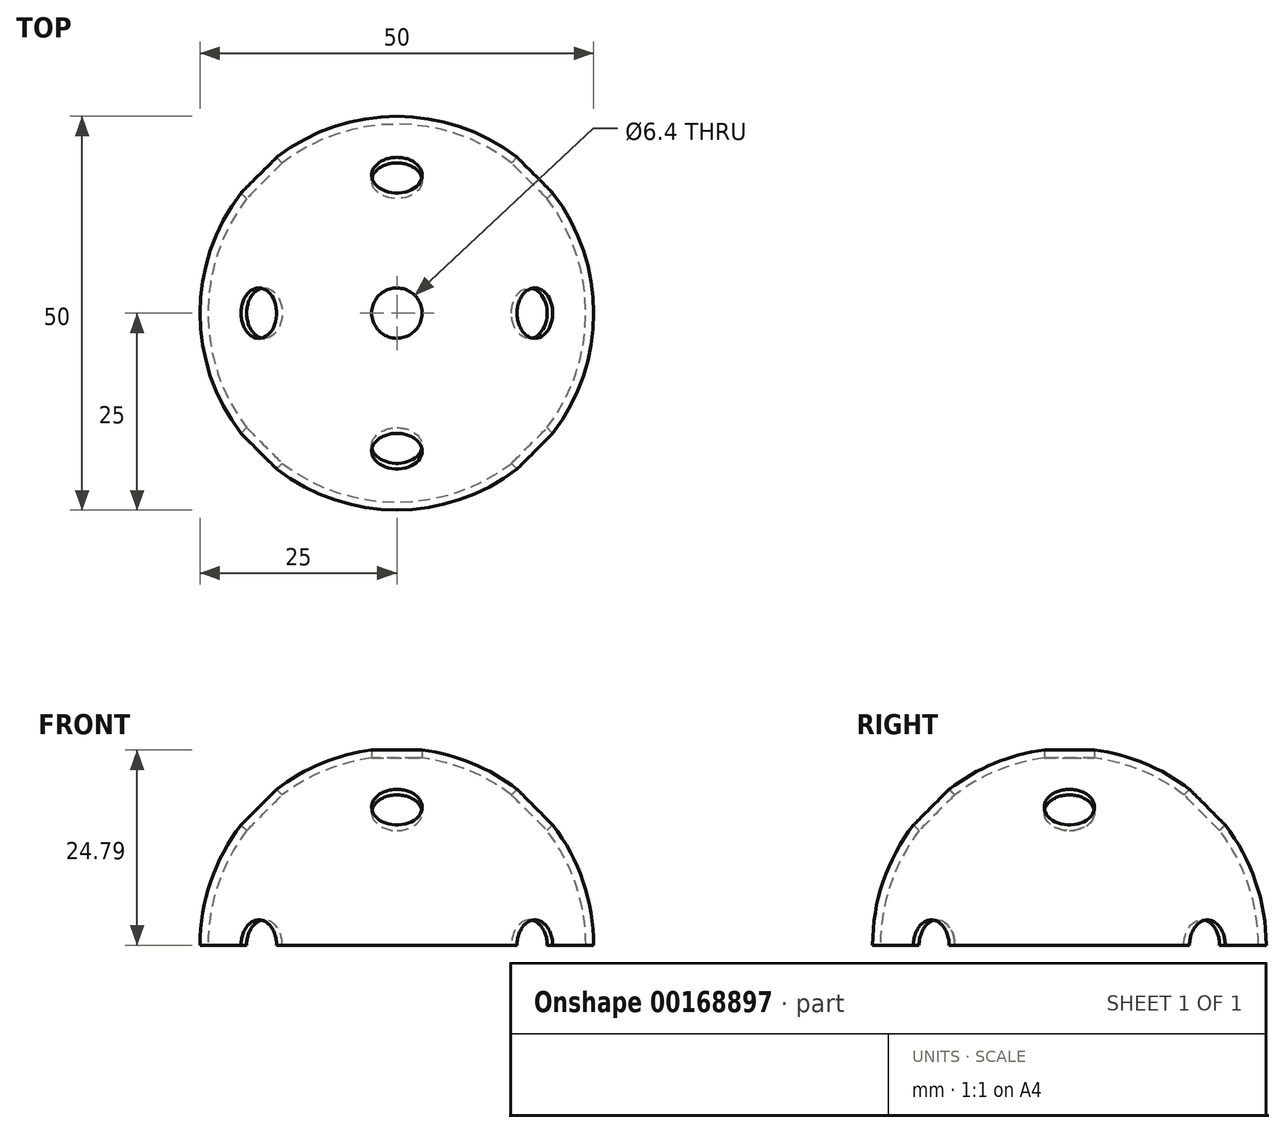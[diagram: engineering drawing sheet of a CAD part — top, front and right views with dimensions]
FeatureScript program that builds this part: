
annotation { "Feature Type Name" : "Feature", "Feature Type Description" : "" }
export const myFeature = defineFeature(function(context is Context, id is Id, definition is map)
    precondition{}
    {
        {
            var Q0;
            Q0=qCreatedBy(makeId("Front.planeOp"),FACE);
            var sketch = newSketch(context, id + "F0", { "sketchPlane" : qUnion([Q0])});
            skLineSegment(sketch, "E0", {"start": v(0, 25) * mm, "end": v(0, 0) * mm});
            skArc(sketch, "E1", {"start": v(0, 25) * mm, "mid": v(17.68, 17.68) * mm, "end": v(25, 0) * mm});
            skLineSegment(sketch, "E2", {"start": v(25, 0) * mm, "end": v(0, 0) * mm});
            skSolve(sketch);
        }
        {
            var Q0;
            Q0=makeQuery(id+"F0.imprint","IMPRINT",FACE,{"disambiguationData":[TD([[makeQuery(id+"F0.imprint","IMPRINT",EDGE,{"derivedFrom":sQuery(id+"F0.wireOp",EDGE,"E0")}),1.0]])]});
            var Q1;
            Q1=sQuery(id+"F0.wireOp",EDGE,"E0");
            revolve(context, id + "F1", {"entities" : qUnion([Q0]), "axis" : qUnion([Q1]), "revolveType" : RevolveType.FULL});
        }
        {
            var Q0;
            Q0=makeQuery(id+"F1.opRevolve","SWEPT_FACE",FACE,{"disambiguationData":[OSD([sQuery(id+"F0.wireOp",EDGE,"E2")])]});
            shell(context, id + "F2", {"entities" : qUnion([Q0]), "thickness" : 1 * mm});
        }
        {
            var Q0;
            Q0=qCreatedBy(makeId("Top.planeOp"),FACE);
            var sketch = newSketch(context, id + "F3", { "sketchPlane" : qUnion([Q0])});
            skCircle(sketch, "E3", {"center": v(0, 0) * mm, "radius": 3.2 * mm});
            skSolve(sketch);
        }
        {
            var Q0;
            Q0=makeQuery(id+"F3.imprint","IMPRINT",FACE,{"disambiguationData":[TD([[makeQuery(id+"F3.imprint","IMPRINT",EDGE,{"derivedFrom":sQuery(id+"F3.wireOp",EDGE,"E3")}),1.0]])]});
            extrude(context, id + "F4", {"entities" : qUnion([Q0]), "operationType" : NewBodyOperationType.REMOVE, "endBound" : BoundingType.THROUGH_ALL, "depth" : 25 * mm});
        }
        {
            var Q0;
            Q0=qCreatedBy(makeId("Right.planeOp"),FACE);
            var Q1;
            Q1=qCreatedBy(makeId("Top.planeOp"),FACE);
            cPlane(context, id + "F5", {"entities" : qUnion([Q0, Q1]), "cplaneType" : CPlaneType.MID_PLANE, "offset" : 25 * mm, "width" : 150 * mm, "height" : 150 * mm});
        }
        {
            var Q0;
            Q0=qCreatedBy(id+"F5.planeOp",FACE);
            var sketch = newSketch(context, id + "F6", { "sketchPlane" : qUnion([Q0])});
            skCircle(sketch, "E4", {"center": v(0, 0) * mm, "radius": 3.2 * mm});
            skSolve(sketch);
        }
        {
            var Q0;
            Q0=makeQuery(id+"F6.imprint","IMPRINT",FACE,{"disambiguationData":[TD([[makeQuery(id+"F6.imprint","IMPRINT",EDGE,{"derivedFrom":sQuery(id+"F6.wireOp",EDGE,"E4")}),1.0]])]});
            extrude(context, id + "F7", {"entities" : qUnion([Q0]), "operationType" : NewBodyOperationType.REMOVE, "endBound" : BoundingType.THROUGH_ALL, "oppositeDirection" : true, "depth" : 25 * mm});
        }
        {
            var Q0;
            Q0=qCreatedBy(makeId("Front.planeOp"),FACE);
            var Q1;
            Q1=qCreatedBy(makeId("Top.planeOp"),FACE);
            cPlane(context, id + "F8", {"entities" : qUnion([Q0, Q1]), "cplaneType" : CPlaneType.MID_PLANE, "offset" : 25 * mm, "width" : 150 * mm, "height" : 150 * mm});
        }
        {
            var Q0;
            Q0=qCreatedBy(id+"F8.planeOp",FACE);
            var sketch = newSketch(context, id + "F9", { "sketchPlane" : qUnion([Q0])});
            skCircle(sketch, "E5", {"center": v(0, 0) * mm, "radius": 3.2 * mm});
            skSolve(sketch);
        }
        {
            var Q0;
            Q0=makeQuery(id+"F9.imprint","IMPRINT",FACE,{"disambiguationData":[TD([[makeQuery(id+"F9.imprint","IMPRINT",EDGE,{"derivedFrom":sQuery(id+"F9.wireOp",EDGE,"E5")}),1.0]])]});
            extrude(context, id + "F10", {"entities" : qUnion([Q0]), "operationType" : NewBodyOperationType.REMOVE, "endBound" : BoundingType.THROUGH_ALL, "oppositeDirection" : true, "depth" : 25 * mm});
        }
        {
            var Q0;
            Q0=qCreatedBy(makeId("Top.planeOp"),FACE);
            var Q1;
            Q1=qCreatedBy(makeId("Right.planeOp"),FACE);
            cPlane(context, id + "F11", {"entities" : qUnion([Q0, Q1]), "cplaneType" : CPlaneType.MID_PLANE, "offset" : 25 * mm, "flipAlignment" : true, "width" : 150 * mm, "height" : 150 * mm});
        }
        {
            var Q0;
            Q0=qCreatedBy(id+"F11.planeOp",FACE);
            var sketch = newSketch(context, id + "F12", { "sketchPlane" : qUnion([Q0])});
            skCircle(sketch, "E6", {"center": v(0, 0) * mm, "radius": 3.2 * mm});
            skSolve(sketch);
        }
        {
            var Q0;
            Q0=makeQuery(id+"F12.imprint","IMPRINT",FACE,{"disambiguationData":[TD([[makeQuery(id+"F12.imprint","IMPRINT",EDGE,{"derivedFrom":sQuery(id+"F12.wireOp",EDGE,"E6")}),1.0]])]});
            extrude(context, id + "F13", {"entities" : qUnion([Q0]), "operationType" : NewBodyOperationType.REMOVE, "endBound" : BoundingType.THROUGH_ALL, "depth" : 25 * mm});
        }
        {
            var Q0;
            Q0=qCreatedBy(makeId("Top.planeOp"),FACE);
            var Q1;
            Q1=qCreatedBy(makeId("Front.planeOp"),FACE);
            cPlane(context, id + "F14", {"entities" : qUnion([Q0, Q1]), "cplaneType" : CPlaneType.MID_PLANE, "offset" : 25 * mm, "flipAlignment" : true, "width" : 150 * mm, "height" : 150 * mm});
        }
        {
            var Q0;
            Q0=qCreatedBy(id+"F14.planeOp",FACE);
            var sketch = newSketch(context, id + "F15", { "sketchPlane" : qUnion([Q0])});
            skCircle(sketch, "E7", {"center": v(0, 0) * mm, "radius": 3.2 * mm});
            skSolve(sketch);
        }
        {
            var Q0;
            Q0=makeQuery(id+"F15.imprint","IMPRINT",FACE,{"disambiguationData":[TD([[makeQuery(id+"F15.imprint","IMPRINT",EDGE,{"derivedFrom":sQuery(id+"F15.wireOp",EDGE,"E7")}),1.0]])]});
            extrude(context, id + "F16", {"entities" : qUnion([Q0]), "operationType" : NewBodyOperationType.REMOVE, "endBound" : BoundingType.THROUGH_ALL, "depth" : 25 * mm});
        }
        {
            var Q0;
            Q0=qCreatedBy(makeId("Front.planeOp"),FACE);
            var Q1;
            Q1=qCreatedBy(makeId("Right.planeOp"),FACE);
            cPlane(context, id + "F17", {"entities" : qUnion([Q0, Q1]), "cplaneType" : CPlaneType.MID_PLANE, "offset" : 25 * mm, "width" : 150 * mm, "height" : 150 * mm});
        }
        {
            var Q0;
            Q0=qCreatedBy(id+"F17.planeOp",FACE);
            var sketch = newSketch(context, id + "F18", { "sketchPlane" : qUnion([Q0])});
            skCircle(sketch, "E8", {"center": v(0, 0) * mm, "radius": 3.2 * mm});
            skSolve(sketch);
        }
        {
            var Q0;
            Q0=makeQuery(id+"F18.imprint","IMPRINT",FACE,{"disambiguationData":[TD([[makeQuery(id+"F18.imprint","IMPRINT",EDGE,{"derivedFrom":sQuery(id+"F18.wireOp",EDGE,"E8")}),1.0]])]});
            extrude(context, id + "F19", {"entities" : qUnion([Q0]), "operationType" : NewBodyOperationType.REMOVE, "endBound" : BoundingType.THROUGH_ALL, "oppositeDirection" : true, "depth" : 25 * mm, "hasSecondDirection" : true, "secondDirectionOppositeDirection" : false, "secondDirectionDepth" : 25 * mm});
        }
        {
            var Q0;
            Q0=qCreatedBy(makeId("Right.planeOp"),FACE);
            var Q1;
            Q1=qCreatedBy(makeId("Front.planeOp"),FACE);
            cPlane(context, id + "F20", {"entities" : qUnion([Q0, Q1]), "cplaneType" : CPlaneType.MID_PLANE, "offset" : 25 * mm, "flipAlignment" : true, "width" : 150 * mm, "height" : 150 * mm});
        }
        {
            var Q0;
            Q0=qCreatedBy(id+"F20.planeOp",FACE);
            var sketch = newSketch(context, id + "F21", { "sketchPlane" : qUnion([Q0])});
            skCircle(sketch, "E9", {"center": v(0, 0) * mm, "radius": 3.2 * mm});
            skSolve(sketch);
        }
        {
            var Q0;
            Q0=makeQuery(id+"F21.imprint","IMPRINT",FACE,{"disambiguationData":[TD([[makeQuery(id+"F21.imprint","IMPRINT",EDGE,{"derivedFrom":sQuery(id+"F21.wireOp",EDGE,"E9")}),1.0]])]});
            extrude(context, id + "F22", {"entities" : qUnion([Q0]), "operationType" : NewBodyOperationType.REMOVE, "endBound" : BoundingType.THROUGH_ALL, "oppositeDirection" : true, "depth" : 25 * mm, "hasSecondDirection" : true, "secondDirectionOppositeDirection" : false, "secondDirectionDepth" : 25 * mm});
        }
    });
